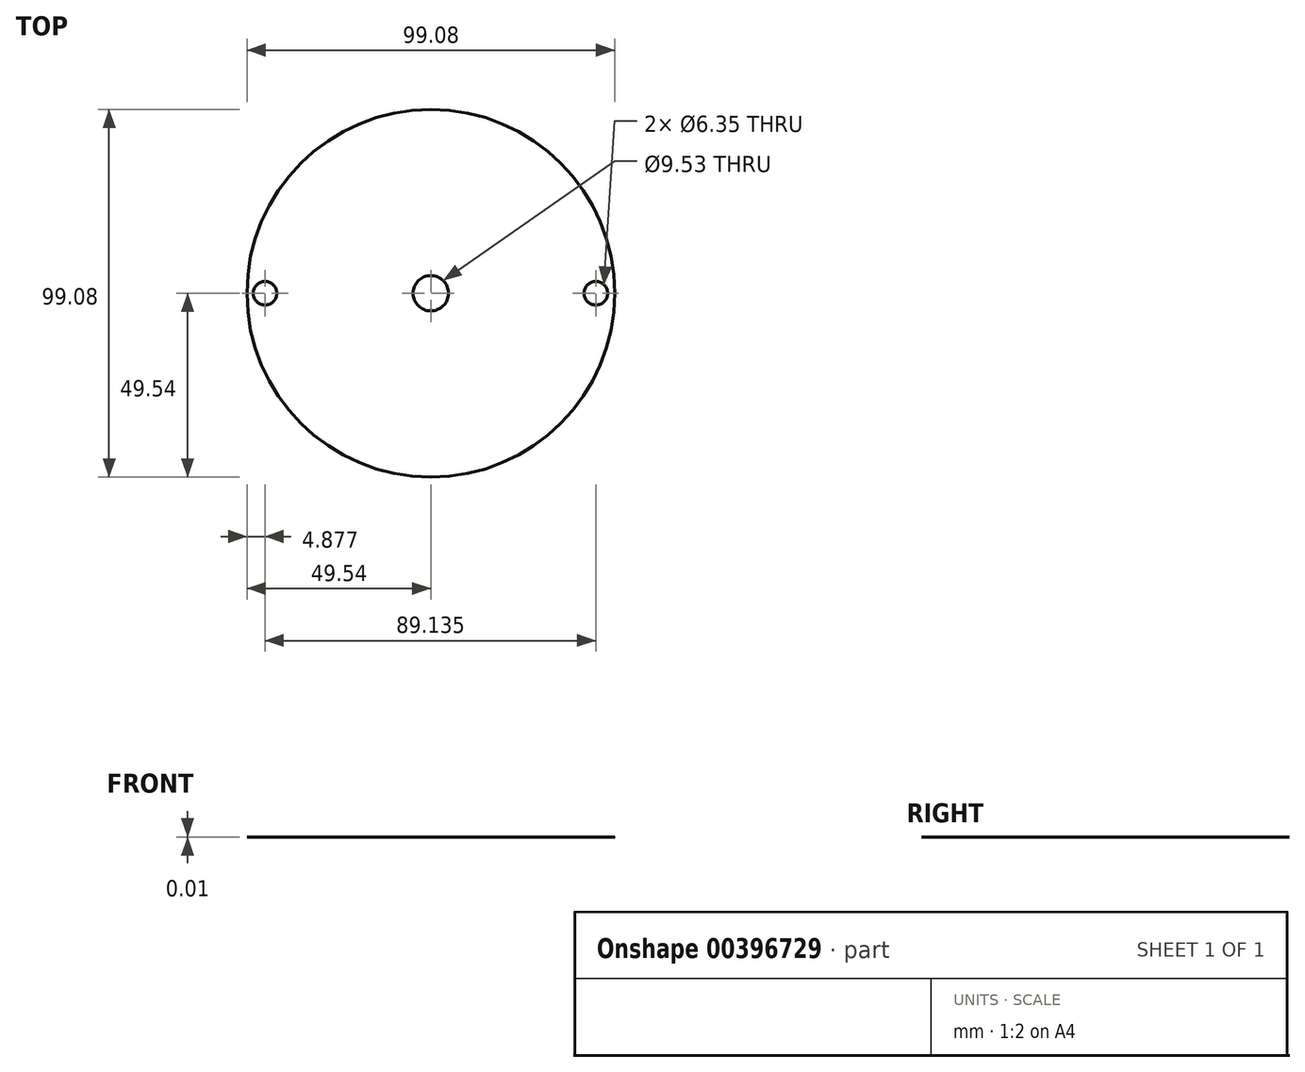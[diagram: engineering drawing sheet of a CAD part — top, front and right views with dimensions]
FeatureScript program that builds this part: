
annotation { "Feature Type Name" : "Feature", "Feature Type Description" : "" }
export const myFeature = defineFeature(function(context is Context, id is Id, definition is map)
    precondition{}
    {
        {
            var Q0;
            Q0=qCreatedBy(makeId("Top.planeOp"),FACE);
            var sketch = newSketch(context, id + "F0", { "sketchPlane" : qUnion([Q0])});
            skCircle(sketch, "E0", {"center": v(0, 0) * mm, "radius": 50.8 * mm});
            skSolve(sketch);
        }
        {
            var Q0;
            Q0 = qSketchRegion(id + "F0", true);
            extrude(context, id + "F1", {"entities" : qUnion([Q0]), "depth" : 1 / 101.6 * mm, "offsetDistance" : 25.4 * mm});
        }
        {
            var Q0;
            Q0=qCreatedBy(makeId("Top.planeOp"),FACE);
            var sketch = newSketch(context, id + "F2", { "sketchPlane" : qUnion([Q0])});
            skCircle(sketch, "E1", {"center": v(0, 0) * mm, "radius": 4.76 * mm});
            skCircle(sketch, "E2", {"center": v(-44.66, 0) * mm, "radius": 3.18 * mm});
            skCircle(sketch, "E3", {"center": v(44.47, 0) * mm, "radius": 3.18 * mm});
            skSolve(sketch);
        }
        {
            var Q0;
            Q0 = qSketchRegion(id + "F2", true);
            extrude(context, id + "F3", {"entities" : qUnion([Q0]), "operationType" : NewBodyOperationType.REMOVE, "depth" : 25.4 * mm, "offsetDistance" : 25.4 * mm});
        }
        {
            var Q0;
            Q0=makeQuery(id+"F1.opExtrude","CAP_EDGE",EDGE,{"disambiguationData":[OSD([sQuery(id+"F0.wireOp",EDGE,"E0")])],"isStart":true});
            chamfer(context, id + "F4", {"entities" : qUnion([Q0]), "width" : 1.27 * mm, "tangentPropagation" : true});
        }
    });
